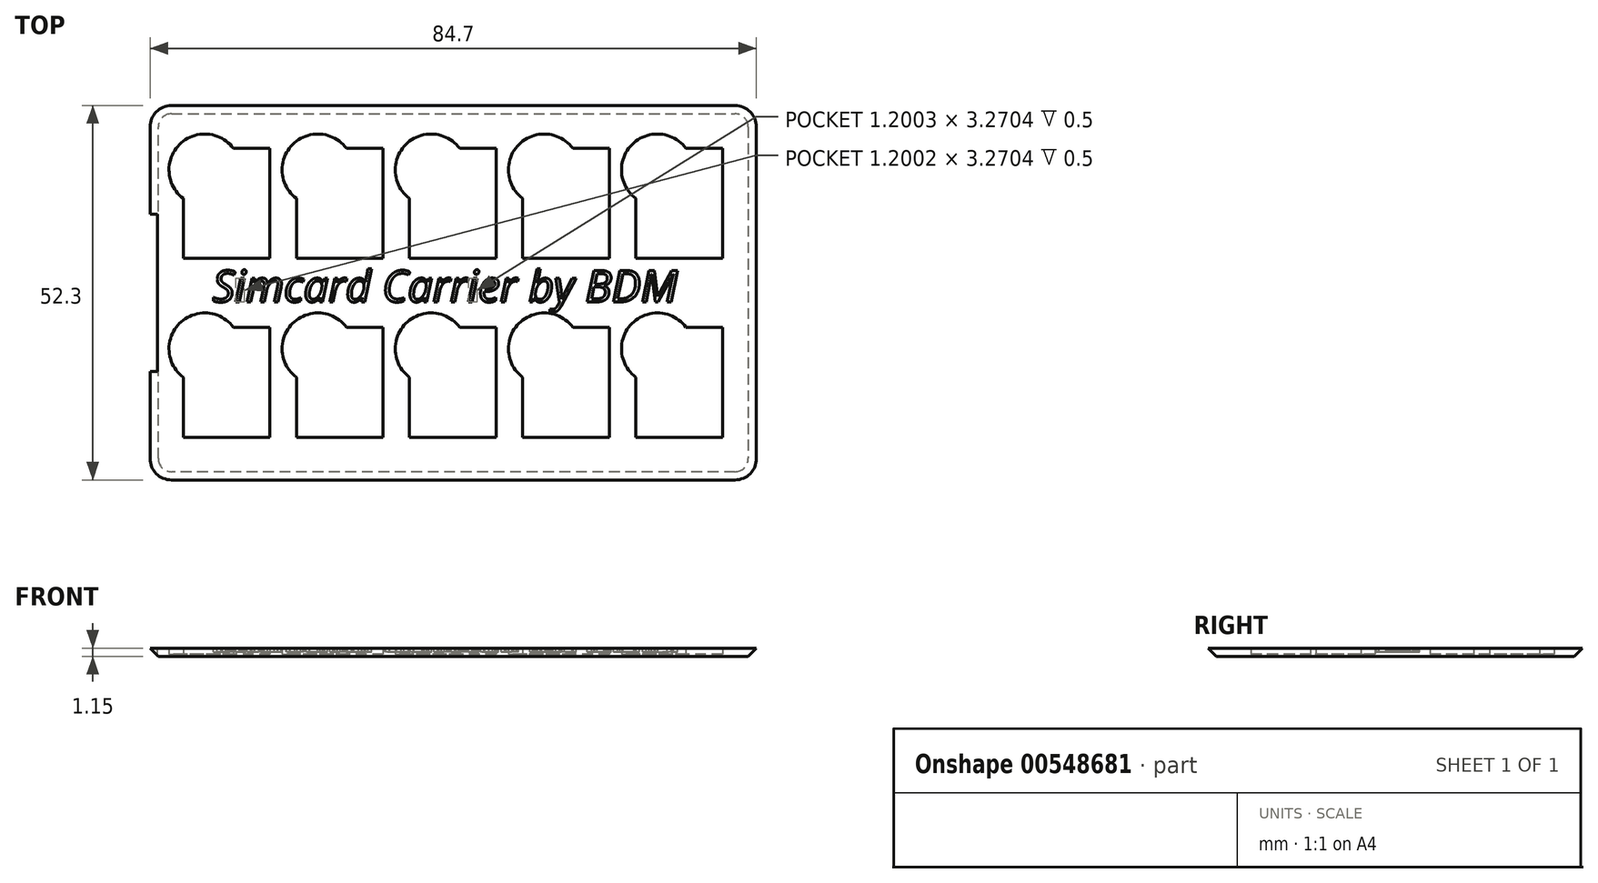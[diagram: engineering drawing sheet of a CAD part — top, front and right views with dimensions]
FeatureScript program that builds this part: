
annotation { "Feature Type Name" : "Feature", "Feature Type Description" : "" }
export const myFeature = defineFeature(function(context is Context, id is Id, definition is map)
    precondition{}
    {
        {
            var Q0;
            Q0=qCreatedBy(makeId("Top.planeOp"),FACE);
            var sketch = newSketch(context, id + "F0", { "sketchPlane" : qUnion([Q0])});
            skLineSegment(sketch, "E0.bottom", {"start": v(3, 0) * mm, "end": v(81.7, 0) * mm});
            skLineSegment(sketch, "E0.top", {"start": v(3, 52.3) * mm, "end": v(81.7, 52.3) * mm});
            skLineSegment(sketch, "E0.left", {"start": v(0, 3) * mm, "end": v(0, 49.3) * mm});
            skLineSegment(sketch, "E0.right", {"start": v(84.7, 3) * mm, "end": v(84.7, 49.3) * mm});
            skPoint(sketch, "E1.visualSharp", {"position": v(0, 0) * mm});
            skArc(sketch, "E1.filletArc", {"start": v(0, 3) * mm, "mid": v(0.88, 0.88) * mm, "end": v(3, 0) * mm});
            skPoint(sketch, "E2.visualSharp", {"position": v(0, 52.3) * mm});
            skArc(sketch, "E2.filletArc", {"start": v(3, 52.3) * mm, "mid": v(0.88, 51.42) * mm, "end": v(0, 49.3) * mm});
            skPoint(sketch, "E3.visualSharp", {"position": v(84.7, 52.3) * mm});
            skArc(sketch, "E3.filletArc", {"start": v(84.7, 49.3) * mm, "mid": v(83.82, 51.42) * mm, "end": v(81.7, 52.3) * mm});
            skPoint(sketch, "E4.visualSharp", {"position": v(84.7, 0) * mm});
            skArc(sketch, "E4.filletArc", {"start": v(81.7, 0) * mm, "mid": v(83.82, 0.88) * mm, "end": v(84.7, 3) * mm});
            skSolve(sketch);
        }
        {
            var Q0;
            Q0=qSketchRegion(id+"F0",true);
            extrude(context, id + "F1", {"entities" : qUnion([Q0]), "depth" : 0.3 * mm, "offsetDistance" : 25 * mm});
        }
        {
            var Q0;
            Q0=makeQuery(id+"F1.opExtrude","CAP_FACE",FACE,{"disambiguationData":[OSD([sQuery(id+"F0.wireOp",EDGE,"E0.bottom"),sQuery(id+"F0.wireOp",EDGE,"E0.top"),sQuery(id+"F0.wireOp",EDGE,"E0.left"),sQuery(id+"F0.wireOp",EDGE,"E0.right")])],"isStart":false});
            var sketch = newSketch(context, id + "F2", { "sketchPlane" : qUnion([Q0])});
            skLineSegment(sketch, "E5.0", {"start": v(3, 52.3) * mm, "end": v(3, 52.3) * mm});
            skPoint(sketch, "E6.0", {"position": v(84.7, 26.15) * mm});
            skLineSegment(sketch, "E7.bottom", {"start": v(16.75, 21.32) * mm, "end": v(16.75, 5.98) * mm});
            skLineSegment(sketch, "E7.top", {"start": v(4.65, 14.33) * mm, "end": v(4.65, 5.98) * mm});
            skLineSegment(sketch, "E7.left", {"start": v(16.75, 21.32) * mm, "end": v(11.65, 21.32) * mm});
            skLineSegment(sketch, "E7.right", {"start": v(16.75, 5.98) * mm, "end": v(4.65, 5.98) * mm});
            skArc(sketch, "E8", {"start": v(11.65, 21.32) * mm, "mid": v(4.11, 21.86) * mm, "end": v(4.65, 14.33) * mm});
            skLineSegment(sketch, "E9.0", {"start": v(0, 3) * mm, "end": v(0, 49.3) * mm});
            skArc(sketch, "E10.0", {"start": v(0, 3) * mm, "mid": v(0.88, 0.88) * mm, "end": v(3, 0) * mm});
            skLineSegment(sketch, "E11.0", {"start": v(3, 0) * mm, "end": v(81.7, 0) * mm});
            skArc(sketch, "E12.0", {"start": v(81.7, 0) * mm, "mid": v(83.82, 0.88) * mm, "end": v(84.7, 3) * mm});
            skLineSegment(sketch, "E13.0", {"start": v(84.7, 3) * mm, "end": v(84.7, 49.3) * mm});
            skLineSegment(sketch, "E14.0", {"start": v(3, 52.3) * mm, "end": v(81.7, 52.3) * mm});
            skArc(sketch, "E15.0", {"start": v(84.7, 49.3) * mm, "mid": v(83.82, 51.42) * mm, "end": v(81.7, 52.3) * mm});
            skArc(sketch, "E16.0", {"start": v(3, 52.3) * mm, "mid": v(0.88, 51.42) * mm, "end": v(0, 49.3) * mm});
            skLineSegment(sketch, "E17.0.1.0", {"start": v(16.75, 46.32) * mm, "end": v(11.65, 46.32) * mm});
            skArc(sketch, "E17.0.1.1", {"start": v(11.65, 46.32) * mm, "mid": v(4.11, 46.86) * mm, "end": v(4.65, 39.32) * mm});
            skLineSegment(sketch, "E17.0.1.2", {"start": v(16.75, 30.97) * mm, "end": v(4.65, 30.97) * mm});
            skLineSegment(sketch, "E17.0.1.3", {"start": v(16.75, 46.32) * mm, "end": v(16.75, 30.98) * mm});
            skLineSegment(sketch, "E17.0.1.4", {"start": v(4.65, 39.32) * mm, "end": v(4.65, 30.97) * mm});
            skLineSegment(sketch, "E17.1.0.0", {"start": v(32.55, 21.32) * mm, "end": v(27.45, 21.32) * mm});
            skArc(sketch, "E17.1.0.1", {"start": v(27.45, 21.32) * mm, "mid": v(19.91, 21.86) * mm, "end": v(20.45, 14.33) * mm});
            skLineSegment(sketch, "E17.1.0.2", {"start": v(32.55, 5.98) * mm, "end": v(20.45, 5.98) * mm});
            skLineSegment(sketch, "E17.1.0.3", {"start": v(32.55, 21.32) * mm, "end": v(32.55, 5.98) * mm});
            skLineSegment(sketch, "E17.1.0.4", {"start": v(20.45, 14.33) * mm, "end": v(20.45, 5.98) * mm});
            skLineSegment(sketch, "E17.1.1.0", {"start": v(32.55, 46.32) * mm, "end": v(27.45, 46.32) * mm});
            skArc(sketch, "E17.1.1.1", {"start": v(27.45, 46.33) * mm, "mid": v(19.91, 46.86) * mm, "end": v(20.45, 39.32) * mm});
            skLineSegment(sketch, "E17.1.1.2", {"start": v(32.55, 30.97) * mm, "end": v(20.45, 30.97) * mm});
            skLineSegment(sketch, "E17.1.1.3", {"start": v(32.55, 46.32) * mm, "end": v(32.55, 30.98) * mm});
            skLineSegment(sketch, "E17.1.1.4", {"start": v(20.45, 39.32) * mm, "end": v(20.45, 30.98) * mm});
            skLineSegment(sketch, "E17.2.0.0", {"start": v(48.35, 21.32) * mm, "end": v(43.25, 21.32) * mm});
            skArc(sketch, "E17.2.0.1", {"start": v(43.25, 21.32) * mm, "mid": v(35.71, 21.86) * mm, "end": v(36.25, 14.33) * mm});
            skLineSegment(sketch, "E17.2.0.2", {"start": v(48.35, 5.98) * mm, "end": v(36.25, 5.98) * mm});
            skLineSegment(sketch, "E17.2.0.3", {"start": v(48.35, 21.32) * mm, "end": v(48.35, 5.98) * mm});
            skLineSegment(sketch, "E17.2.0.4", {"start": v(36.25, 14.33) * mm, "end": v(36.25, 5.98) * mm});
            skLineSegment(sketch, "E17.2.1.0", {"start": v(48.35, 46.32) * mm, "end": v(43.25, 46.32) * mm});
            skArc(sketch, "E17.2.1.1", {"start": v(43.25, 46.32) * mm, "mid": v(35.71, 46.86) * mm, "end": v(36.25, 39.32) * mm});
            skLineSegment(sketch, "E17.2.1.2", {"start": v(48.35, 30.97) * mm, "end": v(36.25, 30.97) * mm});
            skLineSegment(sketch, "E17.2.1.3", {"start": v(48.35, 46.32) * mm, "end": v(48.35, 30.98) * mm});
            skLineSegment(sketch, "E17.2.1.4", {"start": v(36.25, 39.32) * mm, "end": v(36.25, 30.98) * mm});
            skLineSegment(sketch, "E17.3.0.0", {"start": v(64.15, 21.32) * mm, "end": v(59.05, 21.32) * mm});
            skArc(sketch, "E17.3.0.1", {"start": v(59.05, 21.32) * mm, "mid": v(51.51, 21.86) * mm, "end": v(52.05, 14.33) * mm});
            skLineSegment(sketch, "E17.3.0.2", {"start": v(64.15, 5.98) * mm, "end": v(52.05, 5.98) * mm});
            skLineSegment(sketch, "E17.3.0.3", {"start": v(64.15, 21.32) * mm, "end": v(64.15, 5.98) * mm});
            skLineSegment(sketch, "E17.3.0.4", {"start": v(52.05, 14.33) * mm, "end": v(52.05, 5.98) * mm});
            skLineSegment(sketch, "E17.3.1.0", {"start": v(64.15, 46.32) * mm, "end": v(59.05, 46.32) * mm});
            skArc(sketch, "E17.3.1.1", {"start": v(59.05, 46.33) * mm, "mid": v(51.51, 46.86) * mm, "end": v(52.05, 39.32) * mm});
            skLineSegment(sketch, "E17.3.1.2", {"start": v(64.15, 30.97) * mm, "end": v(52.05, 30.97) * mm});
            skLineSegment(sketch, "E17.3.1.3", {"start": v(64.15, 46.32) * mm, "end": v(64.15, 30.98) * mm});
            skLineSegment(sketch, "E17.3.1.4", {"start": v(52.05, 39.32) * mm, "end": v(52.05, 30.98) * mm});
            skLineSegment(sketch, "E17.4.0.0", {"start": v(79.95, 21.32) * mm, "end": v(74.85, 21.32) * mm});
            skArc(sketch, "E17.4.0.1", {"start": v(74.85, 21.32) * mm, "mid": v(67.31, 21.86) * mm, "end": v(67.85, 14.32) * mm});
            skLineSegment(sketch, "E17.4.0.2", {"start": v(79.95, 5.98) * mm, "end": v(67.85, 5.98) * mm});
            skLineSegment(sketch, "E17.4.0.3", {"start": v(79.95, 21.32) * mm, "end": v(79.95, 5.98) * mm});
            skLineSegment(sketch, "E17.4.0.4", {"start": v(67.85, 14.33) * mm, "end": v(67.85, 5.98) * mm});
            skLineSegment(sketch, "E17.4.1.0", {"start": v(79.95, 46.32) * mm, "end": v(74.85, 46.32) * mm});
            skArc(sketch, "E17.4.1.1", {"start": v(74.85, 46.32) * mm, "mid": v(67.31, 46.86) * mm, "end": v(67.85, 39.32) * mm});
            skLineSegment(sketch, "E17.4.1.2", {"start": v(79.95, 30.97) * mm, "end": v(67.85, 30.97) * mm});
            skLineSegment(sketch, "E17.4.1.3", {"start": v(79.95, 46.32) * mm, "end": v(79.95, 30.98) * mm});
            skLineSegment(sketch, "E17.4.1.4", {"start": v(67.85, 39.32) * mm, "end": v(67.85, 30.98) * mm});
            skLineSegment(sketch, "E17.direction1", {"start": v(4.65, 5.98) * mm, "end": v(20.45, 5.98) * mm, "construction": true});
            skLineSegment(sketch, "E17.direction2", {"start": v(4.65, 5.98) * mm, "end": v(4.65, 30.97) * mm, "construction": true});
            skSolve(sketch);
        }
        {
            var Q0;
            Q0=makeQuery(id+"F2.imprint","IMPRINT",FACE,{"disambiguationData":[TD([[makeQuery(id+"F2.imprint","IMPRINT",EDGE,{"derivedFrom":sQuery(id+"F2.wireOp",EDGE,"E5.0")}),-1.0]])]});
            var Q1;
            Q1=makeQuery(id+"F2.imprint","IMPRINT",FACE,{"disambiguationData":[TD([[makeQuery(id+"F2.imprint","IMPRINT",EDGE,{"derivedFrom":sQuery(id+"F2.wireOp",EDGE,"E7.bottom")}),1.0]])]});
            extrude(context, id + "F3", {"entities" : qUnion([Q0, Q1]), "operationType" : NewBodyOperationType.ADD, "depth" : 0.85 * mm, "offsetDistance" : 25 * mm});
        }
        {
            var Q0;
            Q0=makeQuery(id+"F1.opExtrude","CAP_EDGE",EDGE,{"disambiguationData":[OSD([sQuery(id+"F0.wireOp",EDGE,"E0.bottom")])],"isStart":true});
            chamfer(context, id + "F4", {"entities" : qUnion([Q0]), "width" : 1.15 * mm, "tangentPropagation" : true});
        }
        {
            var Q0;
            Q0=makeQuery(id+"F3.opExtrude","CAP_FACE",FACE,{"disambiguationData":[OSD([sQuery(id+"F2.wireOp",EDGE,"E7.bottom"),sQuery(id+"F2.wireOp",EDGE,"E7.top"),sQuery(id+"F2.wireOp",EDGE,"E7.left"),sQuery(id+"F2.wireOp",EDGE,"E7.right"),sQuery(id+"F2.wireOp",EDGE,"E8"),sQuery(id+"F2.wireOp",EDGE,"E9.0"),sQuery(id+"F2.wireOp",EDGE,"E10.0"),sQuery(id+"F2.wireOp",EDGE,"E11.0"),sQuery(id+"F2.wireOp",EDGE,"E12.0"),sQuery(id+"F2.wireOp",EDGE,"E13.0"),sQuery(id+"F2.wireOp",EDGE,"E14.0"),sQuery(id+"F2.wireOp",EDGE,"E15.0"),sQuery(id+"F2.wireOp",EDGE,"E16.0"),sQuery(id+"F2.wireOp",EDGE,"E17.0.1.0"),sQuery(id+"F2.wireOp",EDGE,"E17.0.1.1"),sQuery(id+"F2.wireOp",EDGE,"E17.0.1.2"),sQuery(id+"F2.wireOp",EDGE,"E17.0.1.3"),sQuery(id+"F2.wireOp",EDGE,"E17.0.1.4"),sQuery(id+"F2.wireOp",EDGE,"E17.1.0.0"),sQuery(id+"F2.wireOp",EDGE,"E17.1.0.1"),sQuery(id+"F2.wireOp",EDGE,"E17.1.0.2"),sQuery(id+"F2.wireOp",EDGE,"E17.1.0.3"),sQuery(id+"F2.wireOp",EDGE,"E17.1.0.4"),sQuery(id+"F2.wireOp",EDGE,"E17.1.1.0"),sQuery(id+"F2.wireOp",EDGE,"E17.1.1.1"),sQuery(id+"F2.wireOp",EDGE,"E17.1.1.2"),sQuery(id+"F2.wireOp",EDGE,"E17.1.1.3"),sQuery(id+"F2.wireOp",EDGE,"E17.1.1.4"),sQuery(id+"F2.wireOp",EDGE,"E17.2.0.0"),sQuery(id+"F2.wireOp",EDGE,"E17.2.0.1"),sQuery(id+"F2.wireOp",EDGE,"E17.2.0.2"),sQuery(id+"F2.wireOp",EDGE,"E17.2.0.3"),sQuery(id+"F2.wireOp",EDGE,"E17.2.0.4"),sQuery(id+"F2.wireOp",EDGE,"E17.2.1.0"),sQuery(id+"F2.wireOp",EDGE,"E17.2.1.1"),sQuery(id+"F2.wireOp",EDGE,"E17.2.1.2"),sQuery(id+"F2.wireOp",EDGE,"E17.2.1.3"),sQuery(id+"F2.wireOp",EDGE,"E17.2.1.4"),sQuery(id+"F2.wireOp",EDGE,"E17.3.0.0"),sQuery(id+"F2.wireOp",EDGE,"E17.3.0.1"),sQuery(id+"F2.wireOp",EDGE,"E17.3.0.2"),sQuery(id+"F2.wireOp",EDGE,"E17.3.0.3"),sQuery(id+"F2.wireOp",EDGE,"E17.3.0.4"),sQuery(id+"F2.wireOp",EDGE,"E17.3.1.0"),sQuery(id+"F2.wireOp",EDGE,"E17.3.1.1"),sQuery(id+"F2.wireOp",EDGE,"E17.3.1.2"),sQuery(id+"F2.wireOp",EDGE,"E17.3.1.3"),sQuery(id+"F2.wireOp",EDGE,"E17.3.1.4"),sQuery(id+"F2.wireOp",EDGE,"E17.4.0.0"),sQuery(id+"F2.wireOp",EDGE,"E17.4.0.1"),sQuery(id+"F2.wireOp",EDGE,"E17.4.0.2"),sQuery(id+"F2.wireOp",EDGE,"E17.4.0.3"),sQuery(id+"F2.wireOp",EDGE,"E17.4.0.4"),sQuery(id+"F2.wireOp",EDGE,"E17.4.1.0"),sQuery(id+"F2.wireOp",EDGE,"E17.4.1.1"),sQuery(id+"F2.wireOp",EDGE,"E17.4.1.2"),sQuery(id+"F2.wireOp",EDGE,"E17.4.1.3"),sQuery(id+"F2.wireOp",EDGE,"E17.4.1.4")])],"isStart":false});
            var sketch = newSketch(context, id + "F5", { "sketchPlane" : qUnion([Q0])});
            skLineSegment(sketch, "E18.bottom", {"start": v(0, 37.15) * mm, "end": v(1.05, 37.15) * mm});
            skLineSegment(sketch, "E18.top", {"start": v(0, 15.15) * mm, "end": v(1.05, 15.15) * mm});
            skLineSegment(sketch, "E18.left", {"start": v(0, 37.15) * mm, "end": v(0, 15.15) * mm});
            skLineSegment(sketch, "E18.right", {"start": v(1.05, 37.15) * mm, "end": v(1.05, 15.15) * mm});
            skSolve(sketch);
        }
        {
            var Q0;
            Q0 = qSketchRegion(id + "F5", true);
            extrude(context, id + "F6", {"entities" : qUnion([Q0]), "operationType" : NewBodyOperationType.REMOVE, "oppositeDirection" : true, "depth" : 25 * mm, "offsetDistance" : 25 * mm});
        }
        {
            var Q0;
            Q0=makeQuery(id+"F3.opExtrude","CAP_FACE",FACE,{"disambiguationData":[OSD([sQuery(id+"F2.wireOp",EDGE,"E7.bottom"),sQuery(id+"F2.wireOp",EDGE,"E7.top"),sQuery(id+"F2.wireOp",EDGE,"E7.left"),sQuery(id+"F2.wireOp",EDGE,"E7.right"),sQuery(id+"F2.wireOp",EDGE,"E8"),sQuery(id+"F2.wireOp",EDGE,"E9.0"),sQuery(id+"F2.wireOp",EDGE,"E10.0"),sQuery(id+"F2.wireOp",EDGE,"E11.0"),sQuery(id+"F2.wireOp",EDGE,"E12.0"),sQuery(id+"F2.wireOp",EDGE,"E13.0"),sQuery(id+"F2.wireOp",EDGE,"E14.0"),sQuery(id+"F2.wireOp",EDGE,"E15.0"),sQuery(id+"F2.wireOp",EDGE,"E16.0"),sQuery(id+"F2.wireOp",EDGE,"E17.0.1.0"),sQuery(id+"F2.wireOp",EDGE,"E17.0.1.1"),sQuery(id+"F2.wireOp",EDGE,"E17.0.1.2"),sQuery(id+"F2.wireOp",EDGE,"E17.0.1.3"),sQuery(id+"F2.wireOp",EDGE,"E17.0.1.4"),sQuery(id+"F2.wireOp",EDGE,"E17.1.0.0"),sQuery(id+"F2.wireOp",EDGE,"E17.1.0.1"),sQuery(id+"F2.wireOp",EDGE,"E17.1.0.2"),sQuery(id+"F2.wireOp",EDGE,"E17.1.0.3"),sQuery(id+"F2.wireOp",EDGE,"E17.1.0.4"),sQuery(id+"F2.wireOp",EDGE,"E17.1.1.0"),sQuery(id+"F2.wireOp",EDGE,"E17.1.1.1"),sQuery(id+"F2.wireOp",EDGE,"E17.1.1.2"),sQuery(id+"F2.wireOp",EDGE,"E17.1.1.3"),sQuery(id+"F2.wireOp",EDGE,"E17.1.1.4"),sQuery(id+"F2.wireOp",EDGE,"E17.2.0.0"),sQuery(id+"F2.wireOp",EDGE,"E17.2.0.1"),sQuery(id+"F2.wireOp",EDGE,"E17.2.0.2"),sQuery(id+"F2.wireOp",EDGE,"E17.2.0.3"),sQuery(id+"F2.wireOp",EDGE,"E17.2.0.4"),sQuery(id+"F2.wireOp",EDGE,"E17.2.1.0"),sQuery(id+"F2.wireOp",EDGE,"E17.2.1.1"),sQuery(id+"F2.wireOp",EDGE,"E17.2.1.2"),sQuery(id+"F2.wireOp",EDGE,"E17.2.1.3"),sQuery(id+"F2.wireOp",EDGE,"E17.2.1.4"),sQuery(id+"F2.wireOp",EDGE,"E17.3.0.0"),sQuery(id+"F2.wireOp",EDGE,"E17.3.0.1"),sQuery(id+"F2.wireOp",EDGE,"E17.3.0.2"),sQuery(id+"F2.wireOp",EDGE,"E17.3.0.3"),sQuery(id+"F2.wireOp",EDGE,"E17.3.0.4"),sQuery(id+"F2.wireOp",EDGE,"E17.3.1.0"),sQuery(id+"F2.wireOp",EDGE,"E17.3.1.1"),sQuery(id+"F2.wireOp",EDGE,"E17.3.1.2"),sQuery(id+"F2.wireOp",EDGE,"E17.3.1.3"),sQuery(id+"F2.wireOp",EDGE,"E17.3.1.4"),sQuery(id+"F2.wireOp",EDGE,"E17.4.0.0"),sQuery(id+"F2.wireOp",EDGE,"E17.4.0.1"),sQuery(id+"F2.wireOp",EDGE,"E17.4.0.2"),sQuery(id+"F2.wireOp",EDGE,"E17.4.0.3"),sQuery(id+"F2.wireOp",EDGE,"E17.4.0.4"),sQuery(id+"F2.wireOp",EDGE,"E17.4.1.0"),sQuery(id+"F2.wireOp",EDGE,"E17.4.1.1"),sQuery(id+"F2.wireOp",EDGE,"E17.4.1.2"),sQuery(id+"F2.wireOp",EDGE,"E17.4.1.3"),sQuery(id+"F2.wireOp",EDGE,"E17.4.1.4")])],"isStart":false});
            var sketch = newSketch(context, id + "F7", { "sketchPlane" : qUnion([Q0])});
            skText(sketch, "E19", { "text": "Simcard Carrier by BDM", "fontName": "OpenSans-Italic.ttf"});
            const initialGuessF7  = {"E19": [0.00875, 0.02488, 1, 0, 0.0044]};
            skSetInitialGuess(sketch, initialGuessF7);
            skSolve(sketch);
        }
        {
            var Q0;
            Q0 = qSketchRegion(id + "F7", true);
            extrude(context, id + "F8", {"entities" : qUnion([Q0]), "operationType" : NewBodyOperationType.REMOVE, "oppositeDirection" : true, "depth" : 0.5 * mm, "offsetDistance" : 25 * mm});
        }
    });
